# Revit family: Haworth_CabanaLounge_Table_SquareRectangular_EU_PRELIMINARY
name_source: partatom
category: Furniture
revit_build: Autodesk Revit 2018 (Build: 20170223_1515(x64)
units: mm (PartAtom-declared; Revit-internal decimal feet)

## family parameters
Always vertical = Yes
Cut with Voids When Loaded = No
OmniClass Number = 23.40.70.14.64.21
OmniClass Title = Systems Furniture
Room Calculation Point = No
Shared = No
Work Plane-Based = No

## types (8) — shared parameters
Assembly Code = E2020200
Description = Haworth - Cabana Lounge - Table - Square / Rectangular
Manufacturer = Haworth
Model = SECBX
Revision Number = 1
Size = Verify Final Dim. w/ Haworth
Table Depth = 76 cm
URL = https://www.haworth.com
URL - Product = https://www.haworth.com
Warranty = http://www.haworth.com

## per-type parameters (varying)
| type | Actual Depth | Actual Height | Actual Width | High Screen | Low Screen | No Screen | Rectangle | Screen Width | Square | Table Height | Table Width | With Screen | With Top |
| Square - High Screen | 81 cm | 137 cm | 81 cm | Yes | No | No | No | 81 cm | Yes | 29 cm | 76 cm | Yes | No |
| Square Tiered - No Screen | 76 cm | 40 cm | 76 cm | No | No | Yes | No | 81 cm | Yes | 40 cm | 76 cm | No | Yes |
| Rectangle - High Screen | 81 cm | 137 cm | 58 cm | Yes | No | No | Yes | 58 cm | No | 29 cm | 53 cm | Yes | No |
| Rectangle Tiered - No Screen | 76 cm | 40 cm | 53 cm | No | No | Yes | Yes | 58 cm | No | 40 cm | 53 cm | No | Yes |
| Rectangle - No Screen | 76 cm | 29 cm | 53 cm | No | No | Yes | Yes | 58 cm | No | 29 cm | 53 cm | No | No |
| Rectangle - Low Screen | 81 cm | 107 cm | 58 cm | No | Yes | No | Yes | 58 cm | No | 29 cm | 53 cm | Yes | No |
| Square - Low Screen | 81 cm | 107 cm | 81 cm | No | Yes | No | No | 81 cm | Yes | 29 cm | 76 cm | Yes | No |
| Square - No Screen | 76 cm | 29 cm | 76 cm | No | No | Yes | No | 81 cm | Yes | 29 cm | 76 cm | No | No |

## geometry (parser evidence)
native form markers: Extrusion x1, Sweep x12
no freeform markers — native parametric forms only
